# Revit family: IS_Tipica_T2374_BIM_FR
name_source: partatom
category: Plumbing Fixtures
revit_build: Autodesk Revit 2017 (Build: 20160225_1515(x64)
units: mm (PartAtom-declared; Revit-internal decimal feet)

## family parameters
Always vertical = No
Cut with Voids When Loaded = No
OmniClass Number = 23.45.05.14.21.11
OmniClass Title = Bath/Shower Units
Part Type = Normal
Room Calculation Point = No
Round Connector Dimension = Use Diameter
Shared = No
Work Plane-Based = No

## types (2) — shared parameters
Accessoires = www.idealspec.fr
Auteur = Ideal Standard
BOSUseNativeGeometries = 1
Bim-NomDuProjet = ISI_IdealStandard_ShowerEnclosures_Tipica_T2374
Caractéristiques = TIPICA R Cabine de douche 90 cm verre transparent
CodeBarre = 8014140362326
Conformité = NF
ConseilsDInstallation = 0
Couleur = clair
DateDeCréation = 2018_08_03
Description = TIPICA R Cabine de douche 90 cm verre transparent
Dimensions = 870 x 870 x 1850 mm
EAN code = https://8014140362326
Espace = Interne
Finition = clair
Forme = rectangulaire
Hauteur = 1850 mm
IfcExportAs = Shower enclosures
IfcExportType = IfcSanitaryTerminalType
InformationsProduit = www.idealspec.fr
Largeur = 870 mm
Longueur = 870 mm
Marque = Ideal Standard
Matériel = Glass
Nom = ShowerEnclosures_Tipica_T2374_IdealStandard
PoidsNet = 29,15 KG
Raccordement = Plomberie
Receveur = No
Révision = 1
URL = www.idealspec.fr
Uniclass2015Code = Pr_40_20_06_79
Uniclass2015Title = Shower enclosures
Uniclass2015Version = Products v1.1
UnitéDeMesure = Millimètres
UnitéDeTemps = An
UnitéMonétaire = €
UrlDuFabricant = www.idealspec.fr
Version = 1
zero-valued in all types: Cost, CoûtDeRemplacement, DiamètreÉvacuation, Profondeur

## per-type parameters (varying)
| type | Model |
| T2374YB - TIPICA R CAB. DCHE 90X90 TSP ARG BR 550 | T2374YB |
| T2374AC - TIPICA R CAB 90X90 TRANSP. BLC 550 MM | T2374AC |

## geometry (parser evidence)
native form markers: Sweep x3
no freeform markers — native parametric forms only
